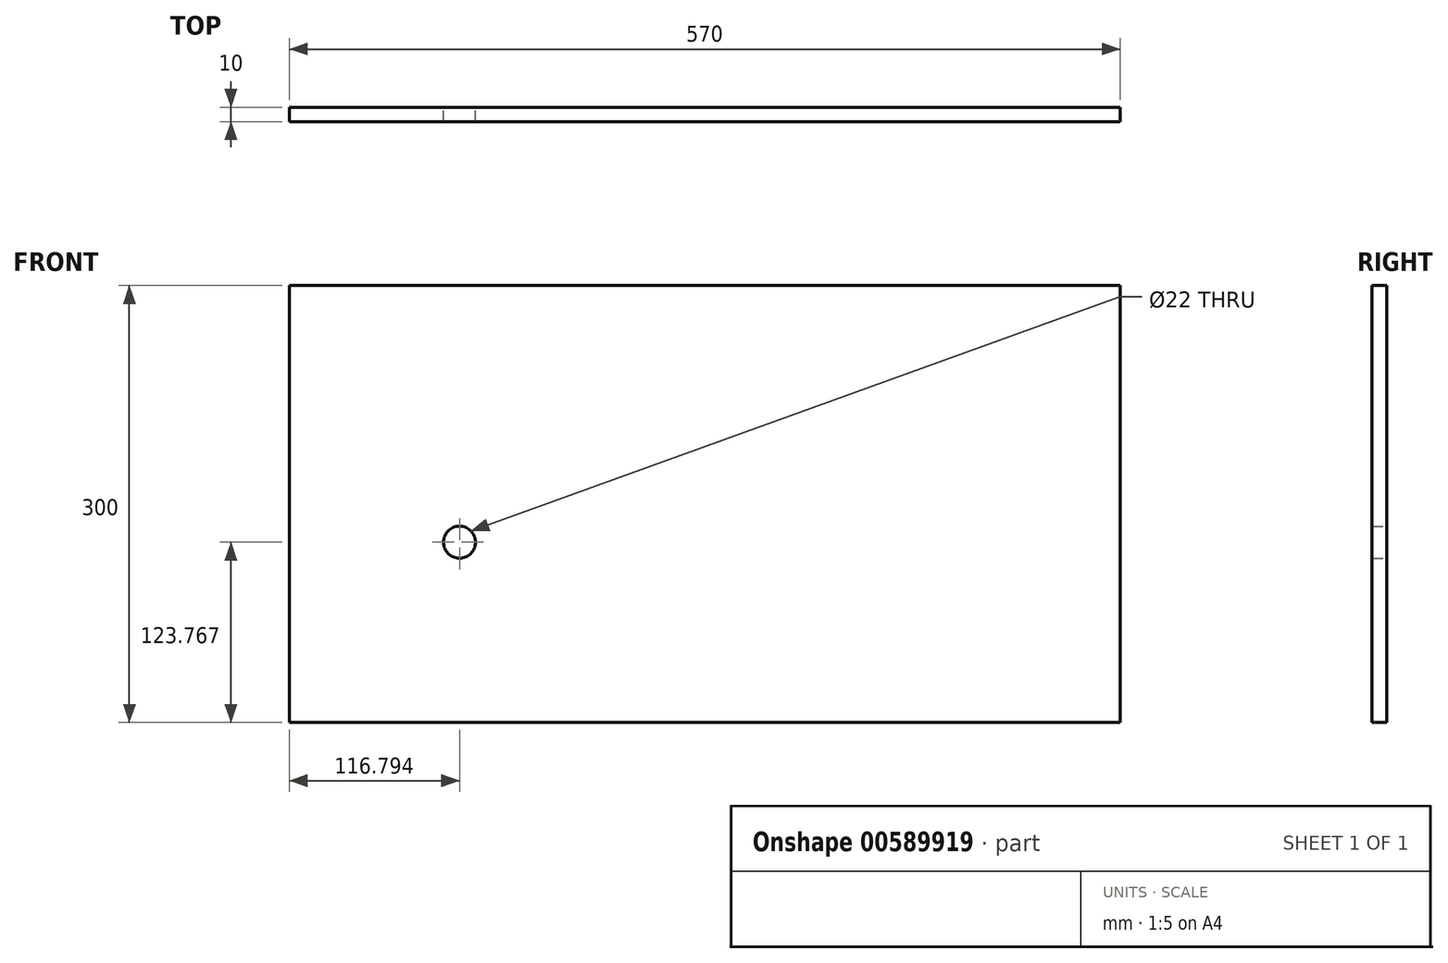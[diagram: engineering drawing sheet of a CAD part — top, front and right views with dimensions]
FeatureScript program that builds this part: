
annotation { "Feature Type Name" : "Feature", "Feature Type Description" : "" }
export const myFeature = defineFeature(function(context is Context, id is Id, definition is map)
    precondition{}
    {
        {
            var Q0;
            Q0=qCreatedBy(makeId("Front.planeOp"),FACE);
            var sketch = newSketch(context, id + "F0", { "sketchPlane" : qUnion([Q0])});
            skLineSegment(sketch, "E0.bottom", {"start": v(-285.66, 145.43) * mm, "end": v(284.34, 145.43) * mm});
            skLineSegment(sketch, "E0.top", {"start": v(-285.66, -154.57) * mm, "end": v(284.34, -154.57) * mm});
            skLineSegment(sketch, "E0.left", {"start": v(-285.66, 145.43) * mm, "end": v(-285.66, -154.57) * mm});
            skLineSegment(sketch, "E0.right", {"start": v(284.34, 145.43) * mm, "end": v(284.34, -154.57) * mm});
            skCircle(sketch, "E1", {"center": v(-168.87, -30.8) * mm, "radius": 100 * mm, "construction": true});
            skCircle(sketch, "E2", {"center": v(-168.87, -30.8) * mm, "radius": 11 * mm});
            skLineSegment(sketch, "E3", {"start": v(-268.2, -142.74) * mm, "end": v(271.18, -142.74) * mm, "construction": true});
            skSolve(sketch);
        }
        {
            var Q0;
            Q0 = qSketchRegion(id + "F0", true);
            extrude(context, id + "F1", {"entities" : qUnion([Q0]), "depth" : 10 * mm, "offsetDistance" : 25 * mm});
        }
    });
